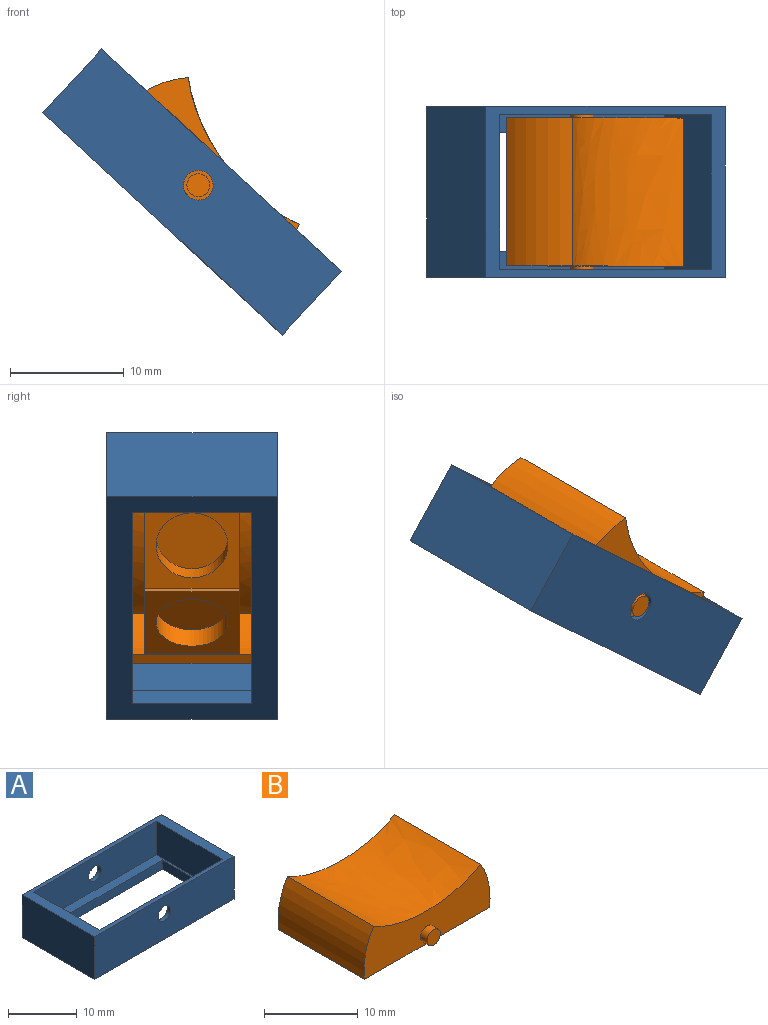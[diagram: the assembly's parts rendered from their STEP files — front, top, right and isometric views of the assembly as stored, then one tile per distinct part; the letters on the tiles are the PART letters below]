
ASSEMBLY  parts=2 mates=1
PART A: 17 faces, bbox 28.7x15x7.6 mm
  f0: plane 28.7x7.62mm, normal (0,-1,0), area 213.4mm2, adj f2,f3,f4,f9,f16
  f1: plane 28.7x7.62mm, normal (0,1,0), area 213.4mm2, adj f2,f3,f4,f10,f16
  f2: plane 15x7.62mm, normal (1,0,0), area 114.3mm2, adj f0,f1,f4,f16
  f3: plane 15x7.62mm, normal (-1,0,0), area 114.3mm2, adj f0,f1,f4,f16
  f4: plane 28.7x15mm, normal (0,0,1), area 86.4mm2, adj f0,f1,f2,f3,f5,f6,f7,f8
  f5: plane 13.6x6mm, normal (-1,0,0), area 81.6mm2, adj f4,f6,f8,f11
  f6: plane 25.3x6mm, normal (0,-1,0), area 146.5mm2, adj f4,f5,f7,f10,f11
  f7: plane 13.6x6mm, normal (1,0,0), area 81.6mm2, adj f4,f6,f8,f11
  f8: plane 25.3x6mm, normal (0,1,0), area 146.5mm2, adj f4,f5,f7,f9,f11
  f9: cylinder r=1.3mm len=2.6mm, axis (0,-1,0), area 5.7mm2, adj f0,f8
  f10: cylinder r=1.3mm len=2.6mm, axis (0,-1,0), area 5.7mm2, adj f1,f6
  f11: plane 25.3x13.6mm, normal (0,0,1), area 84.7mm2, adj f5,f6,f7,f8,f12,f13,f14,f15
  f12: plane 24.7x1.62mm, normal (0,-1,0), area 40mm2, adj f11,f13,f14,f16
  f13: plane 10.5x1.62mm, normal (1,0,0), area 17mm2, adj f11,f12,f15,f16
  f14: plane 10.5x1.62mm, normal (-1,0,0), area 17mm2, adj f11,f12,f15,f16
  f15: plane 24.7x1.62mm, normal (0,1,0), area 40mm2, adj f11,f13,f14,f16
  f16: plane 28.7x15mm, normal (0,0,-1), area 171.2mm2, adj f0,f1,f2,f3,f12,f13,f14,f15
PART B: 27 faces, bbox 19x15x8 mm
  f0: plane 18.83x13mm, normal (0,0,-1), area 59.9mm2, adj f2,f3,f4,f5,f11,f12,f13,f14
  f1: extruded ~16.16x13mm, area 218.8mm2, adj f2,f3,f4,f5
  f2: cylinder r=9.5mm len=13mm, axis (0,1,0), area 85.1mm2, adj f0,f1,f4,f5
  f3: cylinder r=9.5mm len=13mm, axis (0,1,0), area 85.1mm2, adj f0,f1,f4,f5
  f4: plane 19x6.28mm, normal (0,-1,0), area 89.3mm2, adj f0,f1,f2,f3,f8
  f5: plane 19x6.28mm, normal (0,1,0), area 89.3mm2, adj f0,f1,f2,f3,f7
  f6: plane 2x2mm, normal (0,1,0), area 3.1mm2, adj f7
  f7: cylinder r=1mm len=2mm, axis (0,-1,0), area 6.3mm2, adj f5,f6
  f8: cylinder r=1mm len=2mm, axis (0,-1,0), area 6.3mm2, adj f4,f9
  f9: plane 2x2mm, normal (0,-1,0), area 3.1mm2, adj f8
  f10: extruded ~15.35x11mm, area 49.6mm2, adj f11,f12,f13,f14,f17,f18,f21,f22
  f11: cylinder r=8.5mm len=11mm, axis (0,1,0), area 55.6mm2, adj f0,f10,f13,f14
  f12: cylinder r=8.5mm len=11mm, axis (0,1,0), area 55.6mm2, adj f0,f10,f13,f14
  f13: plane 17x4.93mm, normal (0,1,0), area 64.5mm2, adj f0,f10,f11,f12
  f14: plane 17x4.93mm, normal (0,-1,0), area 64.5mm2, adj f0,f10,f11,f12
  f15: plane 8.3x0.93mm, normal (-0.98,0,-0.21), area 7.9mm2, adj f16,f20,f21,f22
  f16: plane 8.3x8.12mm, normal (0.21,0,-0.98), area 37.7mm2, adj f15,f17,f21,f22,f23
  f17: plane 8.3x4.77mm, normal (0.98,0,0.21), area 40.5mm2, adj f10,f16,f21,f22
  f18: plane 8.3x4.77mm, normal (-0.98,0,0.21), area 40.5mm2, adj f10,f19,f21,f22
  f19: plane 8.3x8.12mm, normal (-0.21,0,-0.98), area 37.7mm2, adj f18,f20,f21,f22,f25
  f20: plane 8.3x0.93mm, normal (0.98,0,-0.21), area 7.9mm2, adj f15,f19,f21,f22
  f21: plane 16.63x6.5mm, normal (0,-1,0), area 74.4mm2, adj f10,f15,f16,f17,f18,f19,f20
  f22: plane 16.63x6.5mm, normal (0,1,0), area 74.4mm2, adj f10,f15,f16,f17,f18,f19,f20
  f23: cylinder r=3.15mm len=6.56mm, axis (0.21,0,-0.98), area 37.6mm2, adj f16,f24
  f24: plane 6.3x6.16mm, normal (0.21,0,-0.98), area 31.2mm2, adj f23
  f25: cylinder r=3.15mm len=6.56mm, axis (-0.21,0,-0.98), area 37.6mm2, adj f19,f26
  f26: plane 6.3x6.16mm, normal (-0.21,0,-0.98), area 31.2mm2, adj f25
PLACE A rot(axis=(0,1,0),42.9deg) t=(-3.01,3.85,-2.51)mm
PLACE B rot(axis=(0,1,0),52.9deg) t=(-3.01,3.85,-2.5)mm
MATE revolute B.f7 <-> A.f9  axis (0,-1,0) through (-3.01,-10.15,-2.5)mm
